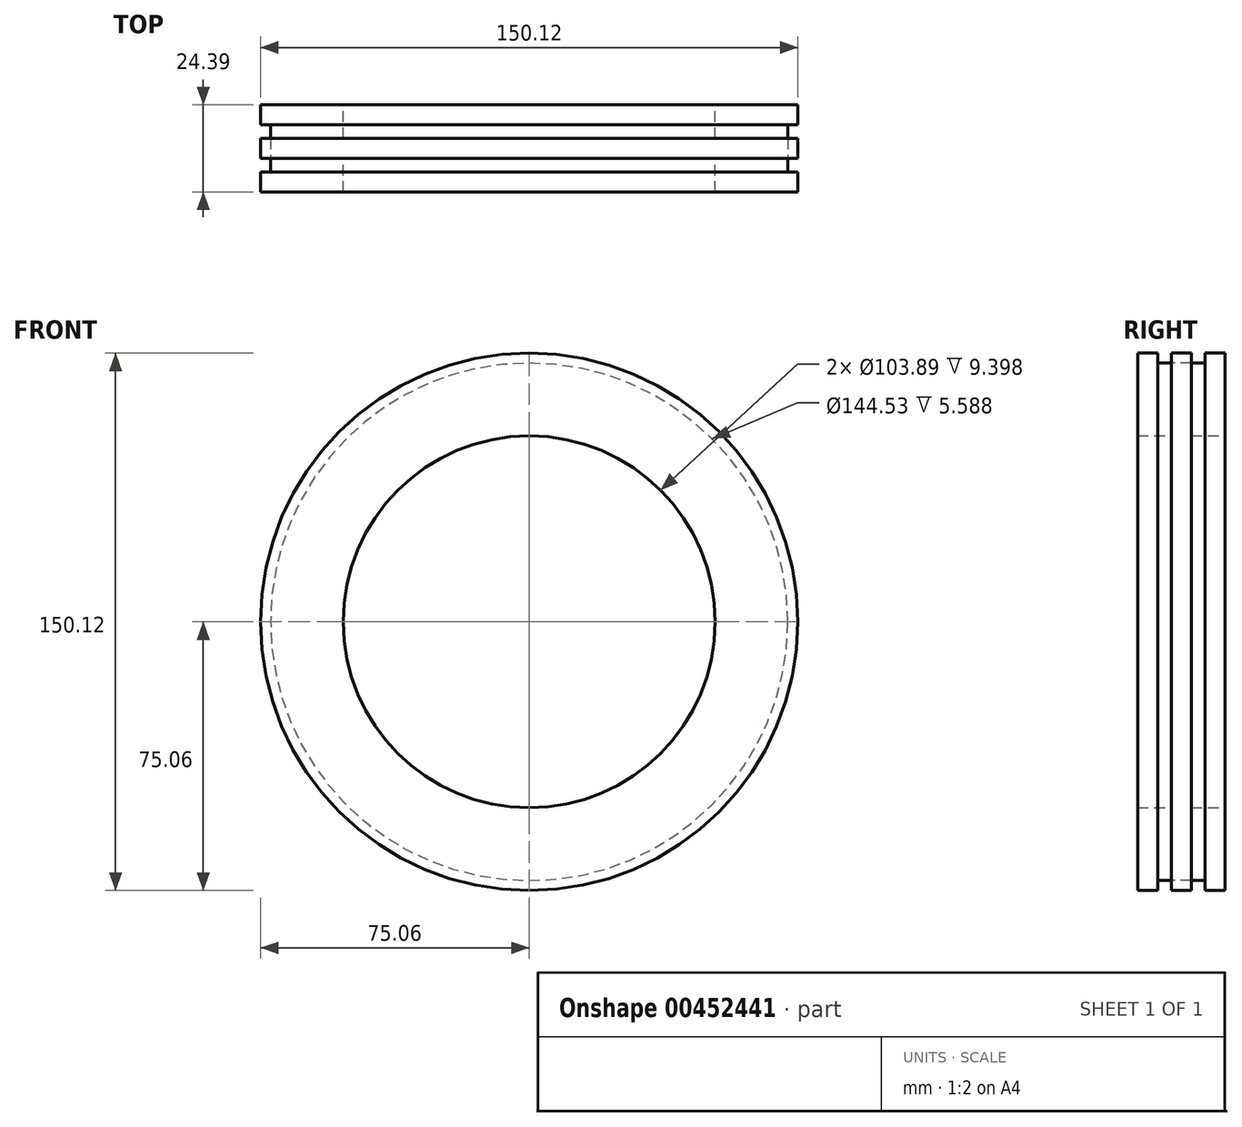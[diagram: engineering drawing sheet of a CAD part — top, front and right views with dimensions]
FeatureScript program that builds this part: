
annotation { "Feature Type Name" : "Feature", "Feature Type Description" : "" }
export const myFeature = defineFeature(function(context is Context, id is Id, definition is map)
    precondition{}
    {
        {
            var Q0;
            Q0=qCreatedBy(makeId("Front.planeOp"),FACE);
            var sketch = newSketch(context, id + "F0", { "sketchPlane" : qUnion([Q0])});
            skCircle(sketch, "E0", {"center": v(0, 0) * mm, "radius": 75.06 * mm});
            skSolve(sketch);
        }
        {
            var Q0;
            Q0=makeQuery(id+"F0.imprint","IMPRINT",FACE,{"disambiguationData":[TD([[makeQuery(id+"F0.imprint","IMPRINT",EDGE,{"derivedFrom":sQuery(id+"F0.wireOp",EDGE,"E0")}),1.0]])]});
            extrude(context, id + "F1", {"entities" : qUnion([Q0]), "depth" : 5.6 * mm});
        }
        {
            var Q0;
            Q0=makeQuery(id+"F1.opExtrude","CAP_FACE",FACE,{"disambiguationData":[OSD([sQuery(id+"F0.wireOp",EDGE,"E0")])],"isStart":true});
            var sketch = newSketch(context, id + "F2", { "sketchPlane" : qUnion([Q0])});
            skCircle(sketch, "E1", {"center": v(0, 0) * mm, "radius": 72.26 * mm});
            skSolve(sketch);
        }
        {
            var Q0;
            Q0=makeQuery(id+"F2.imprint","IMPRINT",FACE,{"disambiguationData":[TD([[makeQuery(id+"F2.imprint","IMPRINT",EDGE,{"derivedFrom":sQuery(id+"F2.wireOp",EDGE,"E1")}),1.0]])]});
            extrude(context, id + "F3", {"entities" : qUnion([Q0]), "operationType" : NewBodyOperationType.ADD, "depth" : 3.8 * mm});
        }
        {
            var Q0;
            Q0=makeQuery(id+"F3.opExtrude","CAP_FACE",FACE,{"disambiguationData":[OSD([sQuery(id+"F2.wireOp",EDGE,"E1")])],"isStart":false});
            var sketch = newSketch(context, id + "F4", { "sketchPlane" : qUnion([Q0])});
            skCircle(sketch, "E2", {"center": v(0, 0) * mm, "radius": 75.06 * mm});
            skSolve(sketch);
        }
        {
            var Q0;
            Q0=makeQuery(id+"F4.imprint","IMPRINT",FACE,{"disambiguationData":[TD([[makeQuery(id+"F4.imprint","IMPRINT",EDGE,{"derivedFrom":sQuery(id+"F4.wireOp",EDGE,"E2")}),1.0]])]});
            extrude(context, id + "F5", {"entities" : qUnion([Q0]), "depth" : 5.6 * mm});
        }
        {
            var Q0;
            Q0=makeQuery(id+"F5.opExtrude","CAP_FACE",FACE,{"disambiguationData":[OSD([sQuery(id+"F2.wireOp",EDGE,"E1"),sQuery(id+"F4.wireOp",EDGE,"E2")])],"isStart":false});
            var sketch = newSketch(context, id + "F6", { "sketchPlane" : qUnion([Q0])});
            skCircle(sketch, "E3", {"center": v(0, 0) * mm, "radius": 72.26 * mm});
            skSolve(sketch);
        }
        {
            var Q0;
            Q0=makeQuery(id+"F6.imprint","IMPRINT",FACE,{"disambiguationData":[TD([[makeQuery(id+"F6.imprint","IMPRINT",EDGE,{"derivedFrom":sQuery(id+"F6.wireOp",EDGE,"E3")}),1.0]])]});
            extrude(context, id + "F7", {"entities" : qUnion([Q0]), "depth" : 3.8 * mm});
        }
        {
            var Q0;
            Q0=makeQuery(id+"F7.opExtrude","CAP_FACE",FACE,{"disambiguationData":[OSD([sQuery(id+"F6.wireOp",EDGE,"E3")])],"isStart":false});
            var sketch = newSketch(context, id + "F8", { "sketchPlane" : qUnion([Q0])});
            skCircle(sketch, "E4", {"center": v(0, 0) * mm, "radius": 75.06 * mm});
            skSolve(sketch);
        }
        {
            var Q0;
            Q0 = qSketchRegion(id + "F8", true);
            extrude(context, id + "F9", {"entities" : qUnion([Q0]), "operationType" : NewBodyOperationType.ADD, "depth" : 5.6 * mm});
        }
        {
            var Q0;
            Q0=makeQuery(id+"F9.opExtrude","CAP_FACE",FACE,{"disambiguationData":[OSD([sQuery(id+"F8.wireOp",EDGE,"E4")])],"isStart":false});
            var sketch = newSketch(context, id + "F10", { "sketchPlane" : qUnion([Q0])});
            skCircle(sketch, "E5", {"center": v(0, 0) * mm, "radius": 51.94 * mm});
            skSolve(sketch);
        }
        {
            var Q0;
            Q0=sQuery(id+"F10.wireOp",VERTEX,"E5.center");
            var Q1;
            Q1=makeQuery(id+"F1.opExtrude","SWEPT_BODY",BODY,{"disambiguationData":[OSD([sQuery(id+"F0.wireOp",EDGE,"E0")])]});
            var Q2;
            Q2=makeQuery(id+"F5.opExtrude","SWEPT_BODY",BODY,{"disambiguationData":[OSD([sQuery(id+"F2.wireOp",EDGE,"E1"),sQuery(id+"F4.wireOp",EDGE,"E2")])]});
            var Q3;
            Q3=makeQuery(id+"F7.opExtrude","SWEPT_BODY",BODY,{"disambiguationData":[OSD([sQuery(id+"F6.wireOp",EDGE,"E3")])]});
            hole(context, id + "F11", {"style" : HoleStyle.SIMPLE, "endStyle" : HoleEndStyle.THROUGH, "holeDiameter" : 103.89 * mm, "isTappedThrough" : true, "tappedDepth" : 12.7 * mm, "tapClearance" : 3, "locations" : qUnion([Q0]), "scope" : qUnion([Q1, Q2, Q3])});
        }
    });
